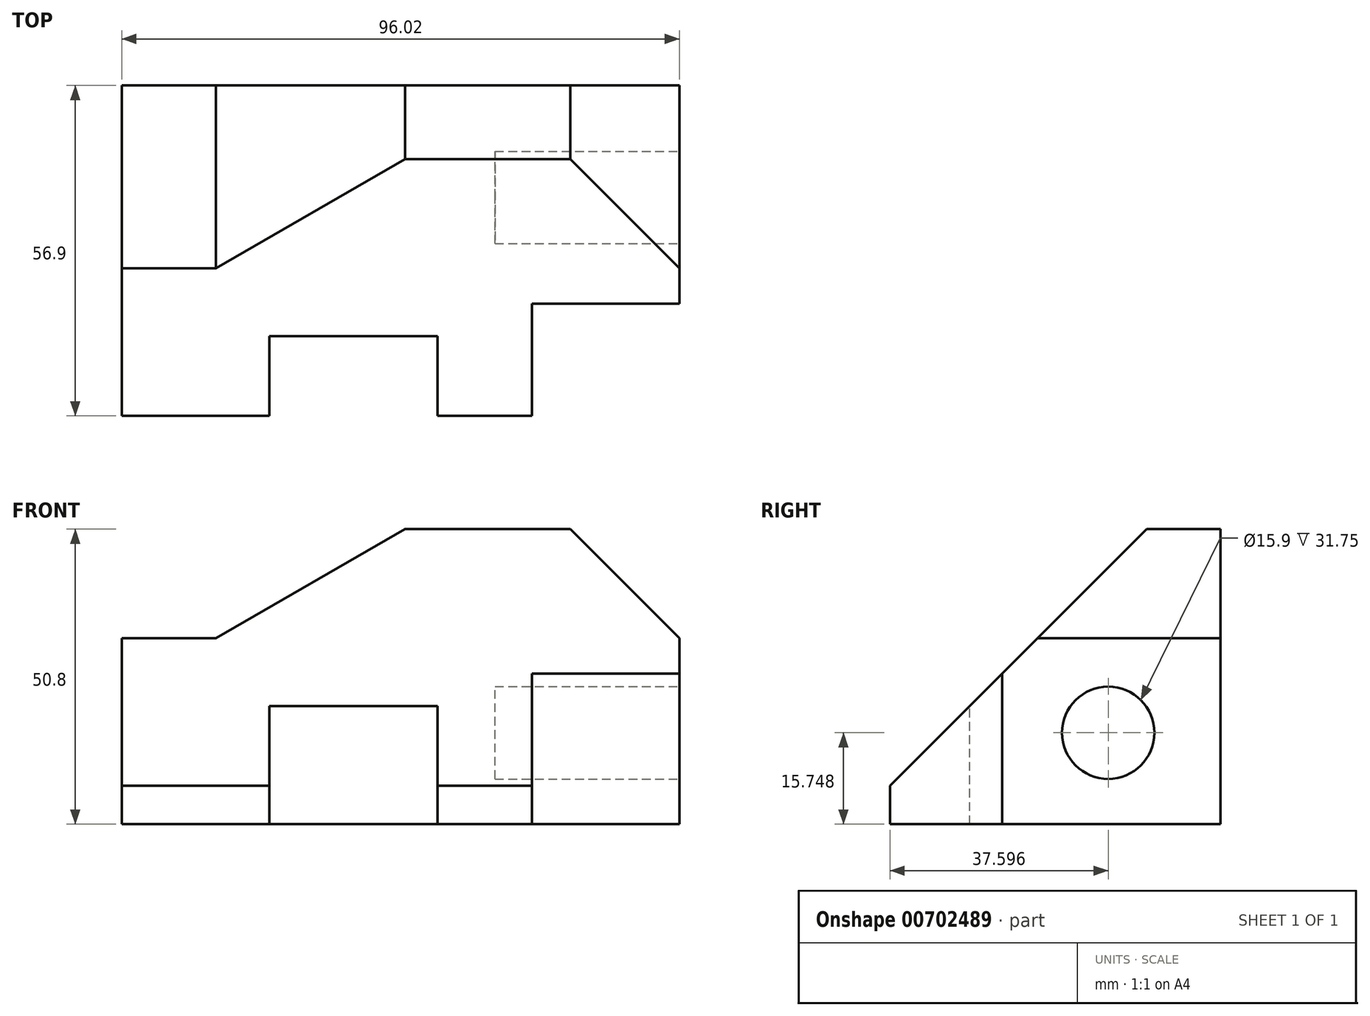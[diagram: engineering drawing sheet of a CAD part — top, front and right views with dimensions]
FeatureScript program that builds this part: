
annotation { "Feature Type Name" : "Feature", "Feature Type Description" : "" }
export const myFeature = defineFeature(function(context is Context, id is Id, definition is map)
    precondition{}
    {
        {
            var Q0;
            Q0=qCreatedBy(makeId("Front.planeOp"),FACE);
            var sketch = newSketch(context, id + "F0", { "sketchPlane" : qUnion([Q0])});
            skLineSegment(sketch, "E0.bottom", {"start": v(48, 25.4) * mm, "end": v(-48, 25.4) * mm});
            skLineSegment(sketch, "E0.top", {"start": v(48, -25.4) * mm, "end": v(-48, -25.4) * mm});
            skLineSegment(sketch, "E0.left", {"start": v(48, 25.4) * mm, "end": v(48, -25.4) * mm});
            skLineSegment(sketch, "E0.right", {"start": v(-48, 25.4) * mm, "end": v(-48, -25.4) * mm});
            skPoint(sketch, "E0.middle", {"position": v(0, 0) * mm});
            skSolve(sketch);
        }
        {
            var Q0;
            Q0=qSketchRegion(id+"F0",true);
            extrude(context, id + "F1", {"entities" : qUnion([Q0]), "depth" : 56.9 * mm});
        }
        {
            var Q0;
            Q0=makeQuery(id+"F1.opExtrude","SWEPT_FACE",FACE,{"disambiguationData":[OSD([sQuery(id+"F0.wireOp",EDGE,"E0.left")])]});
            var sketch = newSketch(context, id + "F2", { "sketchPlane" : qUnion([Q0])});
            skLineSegment(sketch, "E1", {"start": v(-12.7, 25.4) * mm, "end": v(-56.9, -18.8) * mm});
            skLineSegment(sketch, "E2", {"start": v(-56.9, -18.8) * mm, "end": v(-56.9, 25.4) * mm});
            skLineSegment(sketch, "E3", {"start": v(-56.9, 25.4) * mm, "end": v(-12.7, 25.4) * mm});
            skSolve(sketch);
        }
        {
            var Q0;
            Q0=qSketchRegion(id+"F2",true);
            extrude(context, id + "F3", {"entities" : qUnion([Q0]), "operationType" : NewBodyOperationType.REMOVE, "endBound" : BoundingType.THROUGH_ALL, "oppositeDirection" : true, "depth" : 25.4 * mm});
        }
        {
            var Q0;
            Q0=makeQuery(id+"F1.opExtrude","CAP_FACE",FACE,{"disambiguationData":[OSD([sQuery(id+"F0.wireOp",EDGE,"E0.bottom"),sQuery(id+"F0.wireOp",EDGE,"E0.top"),sQuery(id+"F0.wireOp",EDGE,"E0.left"),sQuery(id+"F0.wireOp",EDGE,"E0.right")])],"isStart":false});
            var sketch = newSketch(context, id + "F4", { "sketchPlane" : qUnion([Q0])});
            skLineSegment(sketch, "E4.bottom", {"start": v(-22.6, -25.4) * mm, "end": v(6.35, -25.4) * mm});
            skLineSegment(sketch, "E4.top", {"start": v(-22.6, 5.62) * mm, "end": v(6.35, 5.62) * mm});
            skLineSegment(sketch, "E4.left", {"start": v(-22.6, -25.4) * mm, "end": v(-22.6, 5.62) * mm});
            skLineSegment(sketch, "E4.right", {"start": v(6.35, -25.4) * mm, "end": v(6.35, 5.62) * mm});
            skSolve(sketch);
        }
        {
            var Q0;
            Q0=qSketchRegion(id+"F4",true);
            extrude(context, id + "F5", {"entities" : qUnion([Q0]), "operationType" : NewBodyOperationType.REMOVE, "oppositeDirection" : true, "depth" : 13.72 * mm});
        }
        {
            var Q0;
            {var subQ0=sQuery(id+"F0.wireOp",EDGE,"E0.top");var subQ1=sQuery(id+"F0.wireOp",EDGE,"E0.left");Q0=makeQuery(id+"F5.boolean.opBoolean","SPLIT",FACE,{"disambiguationData":[TD([makeQuery(id+"F1.opExtrude","SWEPT_FACE",FACE,{"disambiguationData":[OSD([subQ1])]})])],"derivedFrom":makeQuery(id+"F1.opExtrude","CAP_FACE",FACE,{"disambiguationData":[OSD([sQuery(id+"F0.wireOp",EDGE,"E0.bottom"),subQ0,subQ1,sQuery(id+"F0.wireOp",EDGE,"E0.right")])],"isStart":false})});}
            var sketch = newSketch(context, id + "F6", { "sketchPlane" : qUnion([Q0])});
            skLineSegment(sketch, "E5.bottom", {"start": v(48, -25.4) * mm, "end": v(22.6, -25.4) * mm});
            skLineSegment(sketch, "E5.top", {"start": v(48, 0) * mm, "end": v(22.6, 0) * mm});
            skLineSegment(sketch, "E5.left", {"start": v(48, -25.4) * mm, "end": v(48, 0) * mm});
            skLineSegment(sketch, "E5.right", {"start": v(22.6, -25.4) * mm, "end": v(22.6, 0) * mm});
            skSolve(sketch);
        }
        {
            var Q0;
            Q0=qSketchRegion(id+"F6",true);
            extrude(context, id + "F7", {"entities" : qUnion([Q0]), "operationType" : NewBodyOperationType.REMOVE, "oppositeDirection" : true, "depth" : 19.3 * mm});
        }
        {
            var Q0;
            Q0=makeQuery(id+"F1.opExtrude","SWEPT_FACE",FACE,{"disambiguationData":[OSD([sQuery(id+"F0.wireOp",EDGE,"E0.left")])]});
            var sketch = newSketch(context, id + "F8", { "sketchPlane" : qUnion([Q0])});
            skCircle(sketch, "E6", {"center": v(-19.3, -9.65) * mm, "radius": 7.95 * mm});
            skSolve(sketch);
        }
        {
            var Q0;
            Q0=qSketchRegion(id+"F8",true);
            extrude(context, id + "F9", {"entities" : qUnion([Q0]), "operationType" : NewBodyOperationType.REMOVE, "oppositeDirection" : true, "depth" : 31.75 * mm});
        }
        {
            var Q0;
            Q0=makeQuery(id+"F1.opExtrude","SWEPT_FACE",FACE,{"disambiguationData":[OSD([sQuery(id+"F0.wireOp",EDGE,"E0.left")])]});
            var sketch = newSketch(context, id + "F10", { "sketchPlane" : qUnion([Q0])});
            skLineSegment(sketch, "E7", {"start": v(-37.6, 0) * mm, "end": v(-37.6, 0.5) * mm});
            skLineSegment(sketch, "E8", {"start": v(-37.6, 0.5) * mm, "end": v(-38.1, 0) * mm});
            skLineSegment(sketch, "E9", {"start": v(-38.1, 0) * mm, "end": v(-37.6, 0) * mm});
            skSolve(sketch);
        }
        {
            var Q0;
            Q0=qSketchRegion(id+"F10",true);
            extrude(context, id + "F11", {"entities" : qUnion([Q0]), "operationType" : NewBodyOperationType.REMOVE, "oppositeDirection" : true, "depth" : 25.4 * mm});
        }
        {
            var Q0;
            Q0=makeQuery(id+"F1.opExtrude","CAP_FACE",FACE,{"disambiguationData":[OSD([sQuery(id+"F0.wireOp",EDGE,"E0.bottom"),sQuery(id+"F0.wireOp",EDGE,"E0.top"),sQuery(id+"F0.wireOp",EDGE,"E0.left"),sQuery(id+"F0.wireOp",EDGE,"E0.right")])],"isStart":true});
            var sketch = newSketch(context, id + "F12", { "sketchPlane" : qUnion([Q0])});
            skLineSegment(sketch, "E10", {"start": v(-48, 25.4) * mm, "end": v(-29.21, 25.4) * mm});
            skLineSegment(sketch, "E11", {"start": v(-29.21, 25.4) * mm, "end": v(-48, 6.6) * mm});
            skLineSegment(sketch, "E12", {"start": v(-48, 6.6) * mm, "end": v(-48, 25.4) * mm});
            skSolve(sketch);
        }
        {
            var Q0;
            Q0=qSketchRegion(id+"F12",true);
            extrude(context, id + "F13", {"entities" : qUnion([Q0]), "operationType" : NewBodyOperationType.REMOVE, "endBound" : BoundingType.THROUGH_ALL, "oppositeDirection" : true, "depth" : 25.4 * mm});
        }
        {
            var Q0;
            Q0=makeQuery(id+"F1.opExtrude","CAP_FACE",FACE,{"disambiguationData":[OSD([sQuery(id+"F0.wireOp",EDGE,"E0.bottom"),sQuery(id+"F0.wireOp",EDGE,"E0.top"),sQuery(id+"F0.wireOp",EDGE,"E0.left"),sQuery(id+"F0.wireOp",EDGE,"E0.right")])],"isStart":true});
            var sketch = newSketch(context, id + "F14", { "sketchPlane" : qUnion([Q0])});
            skLineSegment(sketch, "E13", {"start": v(-0.76, 25.4) * mm, "end": v(31.8, 6.6) * mm});
            skLineSegment(sketch, "E14", {"start": v(31.8, 6.6) * mm, "end": v(48, 6.6) * mm});
            skLineSegment(sketch, "E15", {"start": v(48, 6.6) * mm, "end": v(48, 25.4) * mm});
            skLineSegment(sketch, "E16", {"start": v(48, 25.4) * mm, "end": v(-0.76, 25.4) * mm});
            skSolve(sketch);
        }
        {
            var Q0;
            Q0=qSketchRegion(id+"F14",true);
            extrude(context, id + "F15", {"entities" : qUnion([Q0]), "operationType" : NewBodyOperationType.REMOVE, "endBound" : BoundingType.THROUGH_ALL, "oppositeDirection" : true, "depth" : 25.4 * mm});
        }
    });
